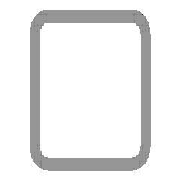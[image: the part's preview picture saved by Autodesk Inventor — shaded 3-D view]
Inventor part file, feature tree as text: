
AUTODESK INVENTOR PART (.ipt)
format: ipt  version: 2025 (Build 290162010, 162A)  size: 134,144 bytes
history: native  units: mm (DEFAULTED — no unit token found)
features: other x4, sketch x1, plane x1
ambient origin geometry x8: Origin, YZ Plane, XZ Plane, XY Plane, X Axis, Y Axis, Z Axis, Center Point
bodies: Solid1 (feature_tree), Body (feature_tree)
feature tree (6):
  parser-record x1  (decoder bookkeeping rows leaked as tree rows — omitted from the tree; the rows remain in map.json)
  other  "Driven Length"
  other  "Start Plane"
  other  "End Plane"
  sketch  "Sketch3"  dims[d3=438.82739mm d4=0.0mm d7=6.0mm d9=80.0mm d11=80.0mm d12=3.0mm d13=40.0mm d14=478.82739mm d15=40.0mm d16=40.0mm d17=90.0deg d18=438.82739mm]
  plane  "Work Plane3"
